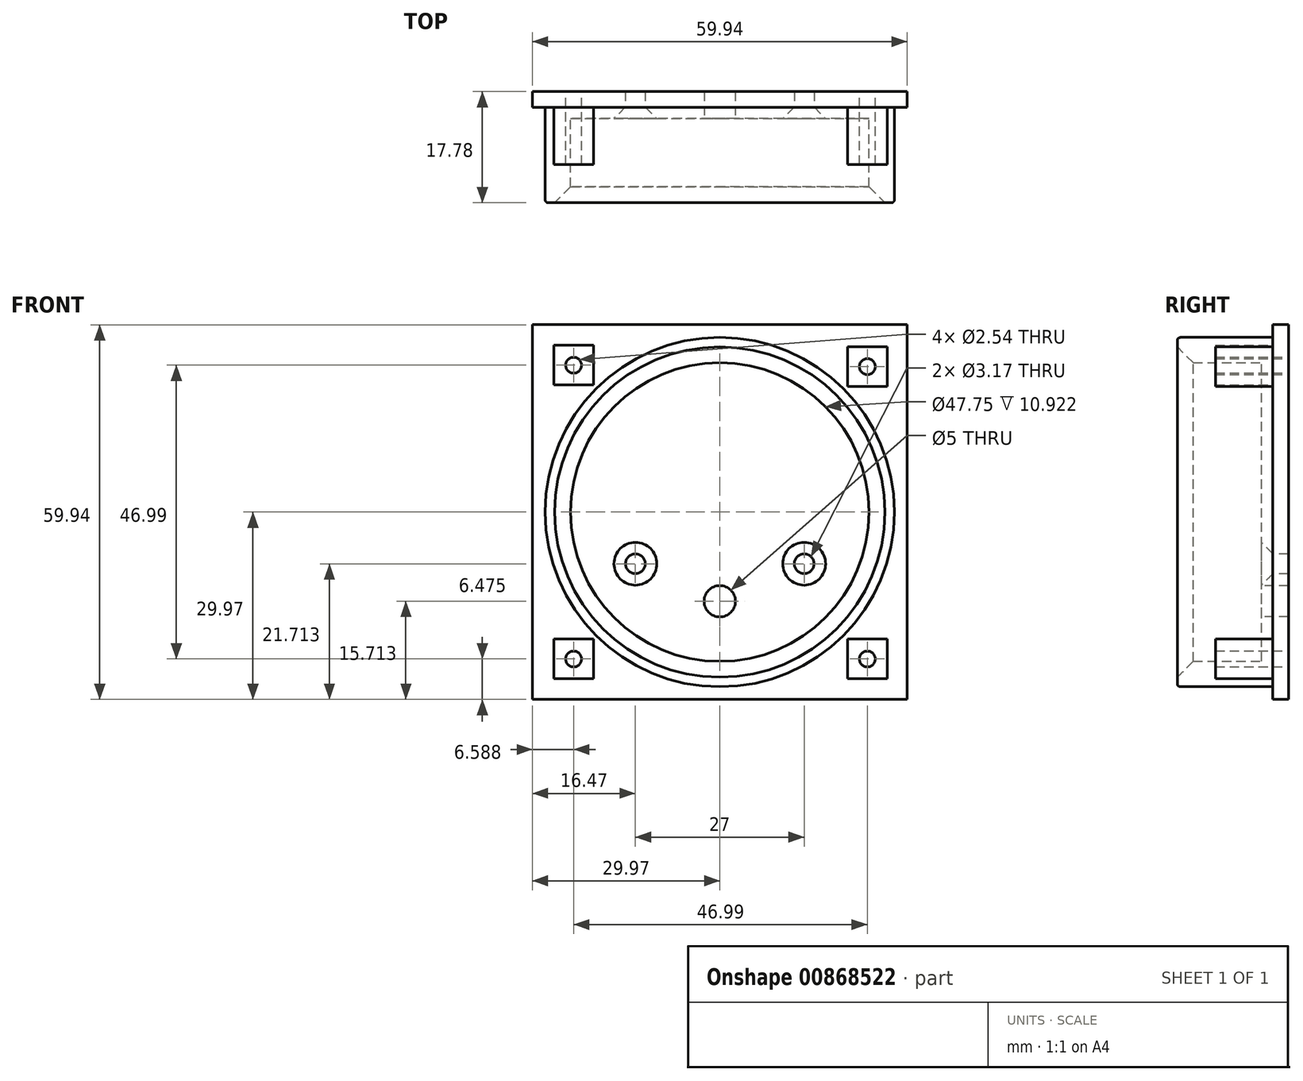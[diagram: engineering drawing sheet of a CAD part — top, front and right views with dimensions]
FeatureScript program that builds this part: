
annotation { "Feature Type Name" : "Feature", "Feature Type Description" : "" }
export const myFeature = defineFeature(function(context is Context, id is Id, definition is map)
    precondition{}
    {
        {
            var Q0;
            Q0=qCreatedBy(makeId("Front.planeOp"),FACE);
            var sketch = newSketch(context, id + "F0", { "sketchPlane" : qUnion([Q0])});
            skCircle(sketch, "E0", {"center": v(0, 0) * mm, "radius": 24.26 * mm});
            skLineSegment(sketch, "E1.bottom", {"start": v(29.97, 29.97) * mm, "end": v(-29.97, 29.97) * mm});
            skLineSegment(sketch, "E1.top", {"start": v(29.97, -29.97) * mm, "end": v(-29.97, -29.97) * mm});
            skLineSegment(sketch, "E1.left", {"start": v(29.97, 29.97) * mm, "end": v(29.97, -29.97) * mm});
            skLineSegment(sketch, "E1.right", {"start": v(-29.97, 29.97) * mm, "end": v(-29.97, -29.97) * mm});
            skPoint(sketch, "E2", {"position": v(-23.38, 23.5) * mm});
            skPoint(sketch, "E3", {"position": v(23.6, 23.27) * mm});
            skPoint(sketch, "E4", {"position": v(23.6, -23.5) * mm});
            skPoint(sketch, "E5", {"position": v(-23.38, -23.5) * mm});
            skLineSegment(sketch, "E6.bottom", {"start": v(-20.2, 26.67) * mm, "end": v(-26.56, 26.67) * mm});
            skLineSegment(sketch, "E6.top", {"start": v(-20.2, 20.32) * mm, "end": v(-26.56, 20.32) * mm});
            skLineSegment(sketch, "E6.left", {"start": v(-20.2, 26.67) * mm, "end": v(-20.2, 20.32) * mm});
            skLineSegment(sketch, "E6.right", {"start": v(-26.56, 26.67) * mm, "end": v(-26.56, 20.32) * mm});
            skLineSegment(sketch, "E7.bottom", {"start": v(26.78, 26.44) * mm, "end": v(20.43, 26.44) * mm});
            skLineSegment(sketch, "E7.top", {"start": v(26.78, 20.1) * mm, "end": v(20.43, 20.1) * mm});
            skLineSegment(sketch, "E7.left", {"start": v(26.78, 26.44) * mm, "end": v(26.78, 20.1) * mm});
            skLineSegment(sketch, "E7.right", {"start": v(20.43, 26.44) * mm, "end": v(20.43, 20.1) * mm});
            skLineSegment(sketch, "E8.bottom", {"start": v(26.78, -20.32) * mm, "end": v(20.43, -20.32) * mm});
            skLineSegment(sketch, "E8.top", {"start": v(26.78, -26.67) * mm, "end": v(20.43, -26.67) * mm});
            skLineSegment(sketch, "E8.left", {"start": v(26.78, -20.32) * mm, "end": v(26.78, -26.67) * mm});
            skLineSegment(sketch, "E8.right", {"start": v(20.43, -20.32) * mm, "end": v(20.43, -26.67) * mm});
            skLineSegment(sketch, "E9.bottom", {"start": v(-20.2, -20.32) * mm, "end": v(-26.56, -20.32) * mm});
            skLineSegment(sketch, "E9.top", {"start": v(-20.2, -26.67) * mm, "end": v(-26.56, -26.67) * mm});
            skLineSegment(sketch, "E9.left", {"start": v(-20.2, -20.32) * mm, "end": v(-20.2, -26.67) * mm});
            skLineSegment(sketch, "E9.right", {"start": v(-26.56, -20.32) * mm, "end": v(-26.56, -26.67) * mm});
            skSolve(sketch);
        }
        {
            var Q0;
            Q0=makeQuery(id+"F0.imprint","IMPRINT",FACE,{"disambiguationData":[TD([[makeQuery(id+"F0.imprint","IMPRINT",EDGE,{"derivedFrom":sQuery(id+"F0.wireOp",EDGE,"E0")}),1.0]])]});
            extrude(context, id + "F1", {"entities" : qUnion([Q0]), "depth" : 4.32 * mm, "offsetDistance" : 25.4 * mm});
        }
        {
            var Q0;
            Q0=qCreatedBy(makeId("Front.planeOp"),FACE);
            var sketch = newSketch(context, id + "F2", { "sketchPlane" : qUnion([Q0])});
            skCircle(sketch, "E10", {"center": v(0, 0) * mm, "radius": 23.88 * mm});
            skCircle(sketch, "E11", {"center": v(0, 0) * mm, "radius": 27.94 * mm});
            skSolve(sketch);
        }
        {
            var Q0;
            Q0=qSketchRegion(id+"F2",true);
            extrude(context, id + "F3", {"entities" : qUnion([Q0]), "operationType" : NewBodyOperationType.ADD, "depth" : 17.78 * mm, "offsetDistance" : 25.4 * mm});
        }
        {
            var Q0;
            Q0=qCreatedBy(makeId("Front.planeOp"),FACE);
            cPlane(context, id + "F4", {"entities" : qUnion([Q0]), "cplaneType" : CPlaneType.OFFSET, "offset" : 2.54 * mm, "width" : 152.4 * mm, "height" : 152.4 * mm});
        }
        {
            var Q0;
            Q0=makeQuery(id+"F0.imprint","IMPRINT",FACE,{"disambiguationData":[TD([[makeQuery(id+"F0.imprint","IMPRINT",EDGE,{"derivedFrom":sQuery(id+"F0.wireOp",EDGE,"E0")}),-1.0]])]});
            extrude(context, id + "F5", {"entities" : qUnion([Q0]), "operationType" : NewBodyOperationType.ADD, "depth" : 2.54 * mm, "offsetDistance" : 25.4 * mm});
        }
        {
            var Q0;
            Q0=makeQuery(id+"F0.imprint","IMPRINT",FACE,{"disambiguationData":[TD([[makeQuery(id+"F0.imprint","IMPRINT",EDGE,{"derivedFrom":sQuery(id+"F0.wireOp",EDGE,"E9.bottom")}),1.0]])]});
            var Q1;
            Q1=makeQuery(id+"F0.imprint","IMPRINT",FACE,{"disambiguationData":[TD([[makeQuery(id+"F0.imprint","IMPRINT",EDGE,{"derivedFrom":sQuery(id+"F0.wireOp",EDGE,"E6.bottom")}),1.0]])]});
            var Q2;
            Q2=makeQuery(id+"F0.imprint","IMPRINT",FACE,{"disambiguationData":[TD([[makeQuery(id+"F0.imprint","IMPRINT",EDGE,{"derivedFrom":sQuery(id+"F0.wireOp",EDGE,"E7.bottom")}),1.0]])]});
            var Q3;
            Q3=makeQuery(id+"F0.imprint","IMPRINT",FACE,{"disambiguationData":[TD([[makeQuery(id+"F0.imprint","IMPRINT",EDGE,{"derivedFrom":sQuery(id+"F0.wireOp",EDGE,"E8.bottom")}),1.0]])]});
            extrude(context, id + "F6", {"entities" : qUnion([Q0, Q1, Q2, Q3]), "operationType" : NewBodyOperationType.ADD, "depth" : 11.68 * mm, "offsetDistance" : 25.4 * mm});
        }
        {
            var Q0;
            Q0=sQuery(id+"F0.wireOp",VERTEX,"E2");
            var Q1;
            Q1=sQuery(id+"F0.wireOp",VERTEX,"E3");
            var Q2;
            Q2=sQuery(id+"F0.wireOp",VERTEX,"E5");
            var Q3;
            Q3=sQuery(id+"F0.wireOp",VERTEX,"E4");
            var Q4;
            Q4=makeQuery(id+"F1.opExtrude","SWEPT_BODY",BODY,{"disambiguationData":[OSD([sQuery(id+"F0.wireOp",EDGE,"E0"),sQuery(id+"F0.wireOp",EDGE,"mUU7OhdX-XNa0-4Drs-y0eB-kvNcseM0QuPt"),sQuery(id+"F0.wireOp",EDGE,"VLppaxhi-9gsj-CoUi-4eyW-4ZfSdwgNkN1v"),sQuery(id+"F0.wireOp",EDGE,"52aOqeBn-3A06-FGgB-2pqV-L4Iadewni0vA"),sQuery(id+"F0.wireOp",EDGE,"DvhnZx25-jBlL-CNyz-VQNl-D04Q6eJg0ANY.bottom"),sQuery(id+"F0.wireOp",EDGE,"DvhnZx25-jBlL-CNyz-VQNl-D04Q6eJg0ANY.top")])]});
            hole(context, id + "F7", {"style" : HoleStyle.SIMPLE, "endStyle" : HoleEndStyle.THROUGH, "oppositeDirection" : true, "holeDiameter" : 2.54 * mm, "majorDiameter" : 6.35 * mm, "isTappedThrough" : true, "tappedDepth" : 12.7 * mm, "tapClearance" : 3, "locations" : qUnion([Q0, Q1, Q2, Q3]), "scope" : qUnion([Q4])});
        }
        {
            var Q0;
            Q0=makeQuery(id+"F3.opExtrude","CAP_EDGE",EDGE,{"disambiguationData":[OSD([sQuery(id+"F2.wireOp",EDGE,"E10")])],"isStart":false});
            chamfer(context, id + "F8", {"entities" : qUnion([Q0]), "width" : 2.54 * mm, "tangentPropagation" : true});
        }
        {
            var Q0;
            Q0=makeQuery(id+"F3.opExtrude","CAP_EDGE",EDGE,{"disambiguationData":[OSD([sQuery(id+"F2.wireOp",EDGE,"E11")])],"isStart":false});
            fillet(context, id + "F9", {"entities" : qUnion([Q0]), "radius" : 0.5 * mm, "tangentPropagation" : true, "allowEdgeOverflow" : false});
        }
        {
            var Q0;
            Q0=makeQuery(id+"F1.opExtrude","CAP_FACE",FACE,{"disambiguationData":[OSD([sQuery(id+"F0.wireOp",EDGE,"E0")])],"isStart":false});
            var sketch = newSketch(context, id + "F10", { "sketchPlane" : qUnion([Q0])});
            skPoint(sketch, "E12", {"position": v(-13.5, -8.26) * mm});
            skPoint(sketch, "E13", {"position": v(13.5, -8.26) * mm});
            skPoint(sketch, "E14", {"position": v(0, -14.26) * mm});
            skSolve(sketch);
        }
        {
            var Q0;
            Q0=sQuery(id+"F10.wireOp",VERTEX,"E12");
            var Q1;
            Q1=sQuery(id+"F10.wireOp",VERTEX,"E13");
            var Q2;
            Q2=makeQuery(id+"F1.opExtrude","SWEPT_BODY",BODY,{"disambiguationData":[OSD([sQuery(id+"F0.wireOp",EDGE,"E0")])]});
            hole(context, id + "F11", {"style" : HoleStyle.C_SINK, "endStyle" : HoleEndStyle.THROUGH, "holeDiameter" : 3.17 * mm, "cSinkDiameter" : 6.86 * mm, "cSinkAngle" : 90 * degree, "majorDiameter" : 6.35 * mm, "isTappedThrough" : true, "tappedDepth" : 12.7 * mm, "tapClearance" : 3, "locations" : qUnion([Q0, Q1]), "scope" : qUnion([Q2])});
        }
        {
            var Q0;
            Q0=sQuery(id+"F10.wireOp",VERTEX,"E14");
            var Q1;
            Q1=makeQuery(id+"F1.opExtrude","SWEPT_BODY",BODY,{"disambiguationData":[OSD([sQuery(id+"F0.wireOp",EDGE,"E0")])]});
            hole(context, id + "F12", {"style" : HoleStyle.SIMPLE, "endStyle" : HoleEndStyle.THROUGH, "holeDiameter" : 5 * mm, "majorDiameter" : 6.35 * mm, "isTappedThrough" : true, "tappedDepth" : 12.7 * mm, "tapClearance" : 3, "locations" : qUnion([Q0]), "scope" : qUnion([Q1])});
        }
    });
